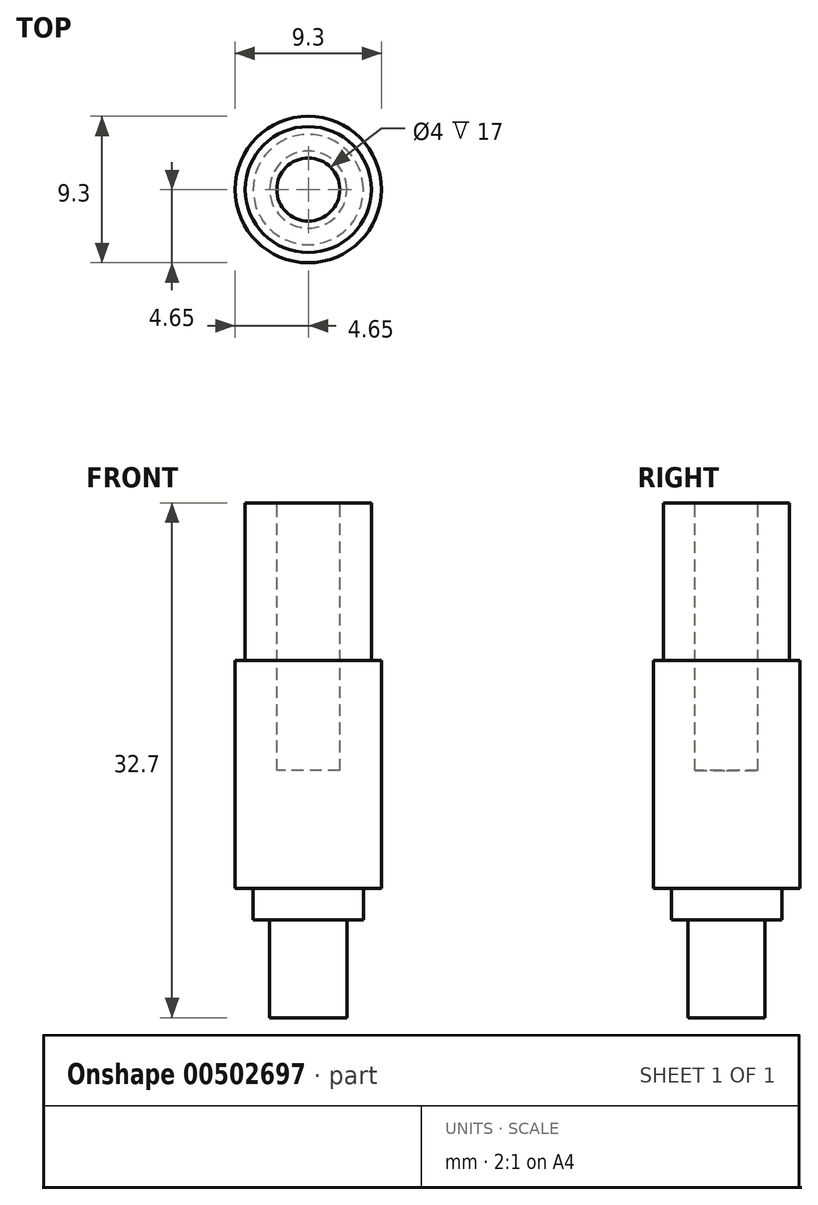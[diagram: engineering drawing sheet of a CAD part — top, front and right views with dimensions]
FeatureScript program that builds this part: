
annotation { "Feature Type Name" : "Feature", "Feature Type Description" : "" }
export const myFeature = defineFeature(function(context is Context, id is Id, definition is map)
    precondition{}
    {
        {
            var Q0;
            Q0=qCreatedBy(makeId("Top.planeOp"),FACE);
            var sketch = newSketch(context, id + "F0", { "sketchPlane" : qUnion([Q0])});
            skCircle(sketch, "E0", {"center": v(0, 0) * mm, "radius": 4.65 * mm});
            skSolve(sketch);
        }
        {
            var Q0;
            Q0 = qSketchRegion(id + "F0", true);
            extrude(context, id + "F1", {"entities" : qUnion([Q0]), "depth" : 14.5 * mm});
        }
        {
            var Q0;
            Q0=makeQuery(id+"F1.opExtrude","CAP_FACE",FACE,{"disambiguationData":[OSD([sQuery(id+"F0.wireOp",EDGE,"E0")])],"isStart":false});
            var sketch = newSketch(context, id + "F2", { "sketchPlane" : qUnion([Q0])});
            skCircle(sketch, "E1", {"center": v(0, 0) * mm, "radius": 4 * mm});
            skSolve(sketch);
        }
        {
            var Q0;
            Q0 = qSketchRegion(id + "F2", true);
            extrude(context, id + "F3", {"entities" : qUnion([Q0]), "operationType" : NewBodyOperationType.ADD, "depth" : 10 * mm});
        }
        {
            var Q0;
            Q0=makeQuery(id+"F3.opExtrude","CAP_FACE",FACE,{"disambiguationData":[OSD([sQuery(id+"F2.wireOp",EDGE,"E1")])],"isStart":false});
            var sketch = newSketch(context, id + "F4", { "sketchPlane" : qUnion([Q0])});
            skCircle(sketch, "E2", {"center": v(0, 0) * mm, "radius": 2 * mm});
            skSolve(sketch);
        }
        {
            var Q0;
            Q0 = qSketchRegion(id + "F4", true);
            extrude(context, id + "F5", {"entities" : qUnion([Q0]), "operationType" : NewBodyOperationType.REMOVE, "oppositeDirection" : true, "depth" : 17 * mm});
        }
        {
            var Q0;
            Q0=makeQuery(id+"F1.opExtrude","CAP_FACE",FACE,{"disambiguationData":[OSD([sQuery(id+"F0.wireOp",EDGE,"E0")])],"isStart":true});
            var sketch = newSketch(context, id + "F6", { "sketchPlane" : qUnion([Q0])});
            skCircle(sketch, "E3", {"center": v(0, 0) * mm, "radius": 3.5 * mm});
            skSolve(sketch);
        }
        {
            var Q0;
            Q0 = qSketchRegion(id + "F6", true);
            extrude(context, id + "F7", {"entities" : qUnion([Q0]), "operationType" : NewBodyOperationType.ADD, "depth" : 2 * mm});
        }
        {
            var Q0;
            Q0=makeQuery(id+"F7.opExtrude","CAP_FACE",FACE,{"disambiguationData":[OSD([sQuery(id+"F6.wireOp",EDGE,"E3")])],"isStart":false});
            var sketch = newSketch(context, id + "F8", { "sketchPlane" : qUnion([Q0])});
            skCircle(sketch, "E4", {"center": v(0, 0) * mm, "radius": 2.45 * mm});
            skSolve(sketch);
        }
        {
            var Q0;
            Q0 = qSketchRegion(id + "F8", true);
            extrude(context, id + "F9", {"entities" : qUnion([Q0]), "operationType" : NewBodyOperationType.ADD, "depth" : 6.2 * mm});
        }
    });
